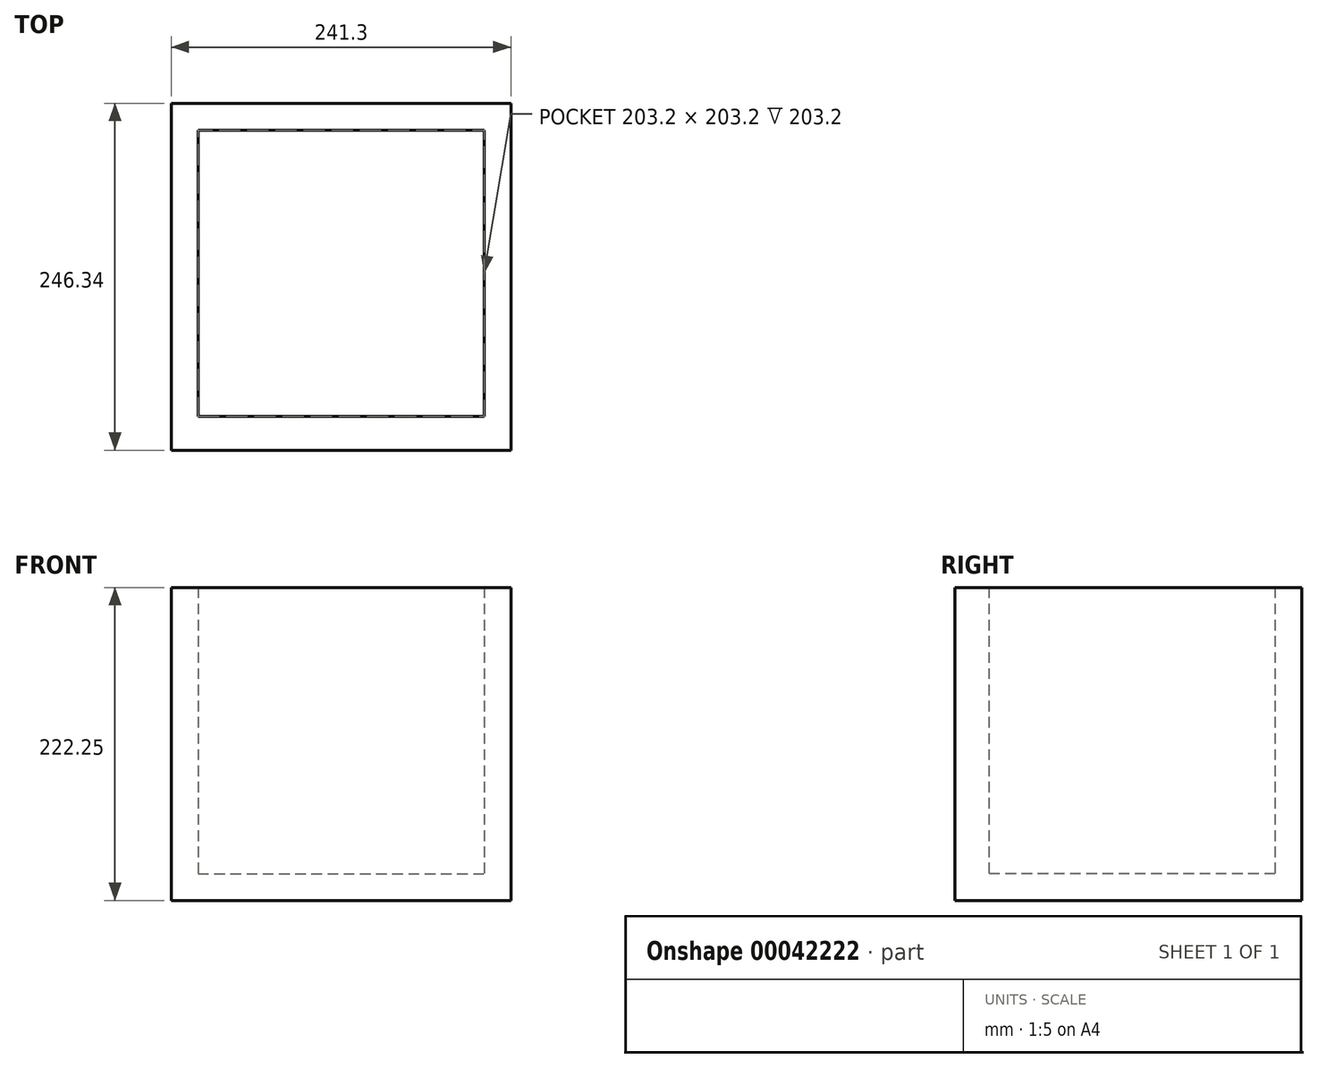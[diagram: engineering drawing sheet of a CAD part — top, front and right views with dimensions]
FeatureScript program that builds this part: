
annotation { "Feature Type Name" : "Feature", "Feature Type Description" : "" }
export const myFeature = defineFeature(function(context is Context, id is Id, definition is map)
    precondition{}
    {
        {
            var Q0;
            Q0=qCreatedBy(makeId("Top.planeOp"),FACE);
            var sketch = newSketch(context, id + "F0", { "sketchPlane" : qUnion([Q0])});
            skLineSegment(sketch, "E0.bottom", {"start": v(-107.1, 94.01) * mm, "end": v(96.1, 94.01) * mm});
            skLineSegment(sketch, "E0.top", {"start": v(-107.1, -109.19) * mm, "end": v(96.1, -109.19) * mm});
            skLineSegment(sketch, "E0.left", {"start": v(-107.1, 94.01) * mm, "end": v(-107.1, -109.19) * mm});
            skLineSegment(sketch, "E0.right", {"start": v(96.1, 94.01) * mm, "end": v(96.1, -109.19) * mm});
            skLineSegment(sketch, "E1.bottom", {"start": v(-126.16, 113.06) * mm, "end": v(115.14, 113.06) * mm});
            skLineSegment(sketch, "E1.top", {"start": v(-126.16, -133.28) * mm, "end": v(115.14, -133.28) * mm});
            skLineSegment(sketch, "E1.left", {"start": v(-126.16, 113.06) * mm, "end": v(-126.16, -133.28) * mm});
            skLineSegment(sketch, "E1.right", {"start": v(115.14, 113.06) * mm, "end": v(115.14, -133.28) * mm});
            skLineSegment(sketch, "E2", {"start": v(-107.1, -9.8) * mm, "end": v(-126.16, -9.8) * mm});
            skLineSegment(sketch, "E3", {"start": v(-2.6, 94.01) * mm, "end": v(-2.6, 113.06) * mm});
            skLineSegment(sketch, "E4", {"start": v(96.1, -7.59) * mm, "end": v(115.14, -7.59) * mm});
            skSolve(sketch);
        }
        {
            var Q0;
            {var subQ1=sQuery(id+"F0.wireOp",EDGE,"E0.top");Q0=makeQuery(id+"F0.imprint","IMPRINT",FACE,{"disambiguationData":[TD([[makeQuery(id+"F0.imprint","IMPRINT",EDGE,{"derivedFrom":subQ1}),-1.0]])]});}
            var Q1;
            {var subQ3=sQuery(id+"F0.wireOp",EDGE,"E2");Q1=makeQuery(id+"F0.imprint","IMPRINT",FACE,{"disambiguationData":[TD([[makeQuery(id+"F0.imprint","IMPRINT",EDGE,{"derivedFrom":subQ3}),-1.0]])]});}
            var Q2;
            {var subQ7=sQuery(id+"F0.wireOp",EDGE,"E3");Q2=makeQuery(id+"F0.imprint","IMPRINT",FACE,{"disambiguationData":[TD([[makeQuery(id+"F0.imprint","IMPRINT",EDGE,{"derivedFrom":subQ7}),-1.0]])]});}
            extrude(context, id + "F1", {"entities" : qUnion([Q0, Q1, Q2]), "depth" : 203.2 * mm});
        }
        {
            var Q0;
            Q0=makeQuery(id+"F1.opExtrude","CAP_FACE",FACE,{"disambiguationData":[OSD([sQuery(id+"F0.wireOp",EDGE,"E0.bottom"),sQuery(id+"F0.wireOp",EDGE,"E0.top"),sQuery(id+"F0.wireOp",EDGE,"E0.left"),sQuery(id+"F0.wireOp",EDGE,"E0.right"),sQuery(id+"F0.wireOp",EDGE,"E1.bottom"),sQuery(id+"F0.wireOp",EDGE,"E1.top"),sQuery(id+"F0.wireOp",EDGE,"E1.left"),sQuery(id+"F0.wireOp",EDGE,"E1.right")])],"isStart":true});
            var sketch = newSketch(context, id + "F2", { "sketchPlane" : qUnion([Q0])});
            skLineSegment(sketch, "E5.bottom", {"start": v(-126.16, 133.28) * mm, "end": v(115.14, 133.28) * mm});
            skLineSegment(sketch, "E5.top", {"start": v(-126.16, -113.06) * mm, "end": v(115.14, -113.06) * mm});
            skLineSegment(sketch, "E5.left", {"start": v(-126.16, 133.28) * mm, "end": v(-126.16, -113.06) * mm});
            skLineSegment(sketch, "E5.right", {"start": v(115.14, 133.28) * mm, "end": v(115.14, -113.06) * mm});
            skSolve(sketch);
        }
        {
            var Q0;
            Q0 = qSketchRegion(id + "F2", true);
            extrude(context, id + "F3", {"entities" : qUnion([Q0]), "operationType" : NewBodyOperationType.ADD, "depth" : 19.05 * mm});
        }
    });
